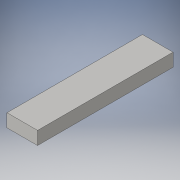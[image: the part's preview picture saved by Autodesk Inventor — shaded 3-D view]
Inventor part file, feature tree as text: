
AUTODESK INVENTOR PART (.ipt)
format: ipt  version: 2016 (Build 200138000, 138)  size: 86,528 bytes
history: native  units: in
note: dims shown in document units (in); Inventor stores cm internally (conversion verified against a paired STEP export)
features: extrude x1, sketch x1
ambient origin geometry x8: Origin, YZ Plane, XZ Plane, XY Plane, X Axis, Y Axis, Z Axis, Center Point
bodies: Solid1 (feature_tree)
feature tree (2):
  extrude  "Extrusion1"  Depth=1.5in TaperAngle=0.0deg
  sketch  "Sketch1"  dims[d0=3.5in d2=1.5in d3=0.0in]
